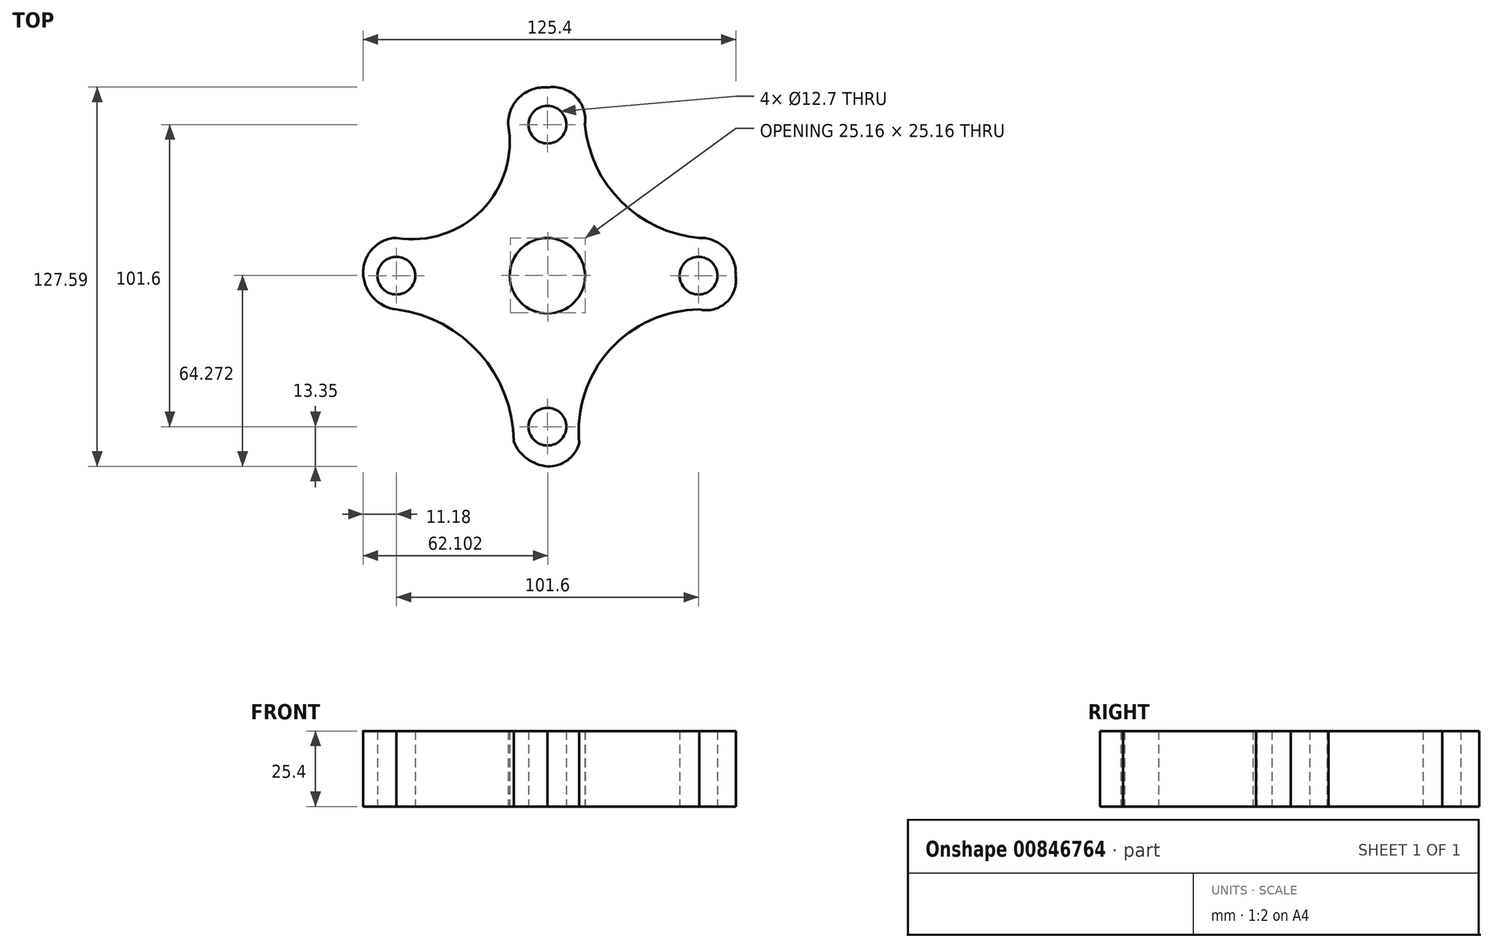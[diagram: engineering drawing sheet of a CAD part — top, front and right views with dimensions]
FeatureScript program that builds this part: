
annotation { "Feature Type Name" : "Feature", "Feature Type Description" : "" }
export const myFeature = defineFeature(function(context is Context, id is Id, definition is map)
    precondition{}
    {
        {
            var Q0;
            Q0=qCreatedBy(makeId("Top.planeOp"),FACE);
            var sketch = newSketch(context, id + "F0", { "sketchPlane" : qUnion([Q0])});
            skCircle(sketch, "E0", {"center": v(0, 0) * mm, "radius": 12.7 * mm});
            skLineSegment(sketch, "E1", {"start": v(0, 0) * mm, "end": v(50.8, 0) * mm});
            skLineSegment(sketch, "E2", {"start": v(0, 0) * mm, "end": v(-50.8, 0) * mm});
            skCircle(sketch, "E3", {"center": v(-50.8, 0) * mm, "radius": 6.35 * mm});
            skCircle(sketch, "E4", {"center": v(50.8, 0) * mm, "radius": 6.35 * mm});
            skLineSegment(sketch, "E5", {"start": v(0, 0) * mm, "end": v(0, 50.8) * mm});
            skLineSegment(sketch, "E6", {"start": v(0, 0) * mm, "end": v(0, -50.8) * mm});
            skCircle(sketch, "E7", {"center": v(0, 50.8) * mm, "radius": 6.35 * mm});
            skCircle(sketch, "E8", {"center": v(0, -50.8) * mm, "radius": 6.35 * mm});
            skArc(sketch, "E9", {"start": v(50.8, 0) * mm, "mid": v(47.62, -0.1) * mm, "end": v(44.46, -0.4) * mm});
            skArc(sketch, "E10.trimOffspring", {"start": v(0.4, -44.46) * mm, "mid": v(0.1, -47.62) * mm, "end": v(0, -50.8) * mm});
            skArc(sketch, "E11", {"start": v(-11.37, -55.83) * mm, "mid": v(-6.84, -61.57) * mm, "end": v(0, -64.15) * mm});
            skArc(sketch, "E12", {"start": v(0, -64.15) * mm, "mid": v(6.7, -62.1) * mm, "end": v(10.7, -56.34) * mm});
            skArc(sketch, "E13", {"start": v(51.08, -11.37) * mm, "mid": v(20.97, -24.95) * mm, "end": v(10.7, -56.34) * mm});
            skArc(sketch, "E14", {"start": v(51.08, -11.37) * mm, "mid": v(60.21, -8.94) * mm, "end": v(63.3, 0) * mm});
            skArc(sketch, "E15", {"start": v(63.3, 0) * mm, "mid": v(59.98, 9.05) * mm, "end": v(51.08, 12.73) * mm});
            skArc(sketch, "E16", {"start": v(12.56, 50.9) * mm, "mid": v(24.87, 24.81) * mm, "end": v(51.08, 12.73) * mm});
            skArc(sketch, "E17", {"start": v(12.56, 50.9) * mm, "mid": v(9.44, 60.3) * mm, "end": v(0, 63.3) * mm});
            skArc(sketch, "E18", {"start": v(0, 63.3) * mm, "mid": v(-9.38, 60.05) * mm, "end": v(-13.24, 50.9) * mm});
            skArc(sketch, "E19", {"start": v(-50.74, 12.73) * mm, "mid": v(-22.04, 22.04) * mm, "end": v(-13.24, 50.9) * mm});
            skArc(sketch, "E20", {"start": v(-50.74, 12.73) * mm, "mid": v(-59.07, 8.76) * mm, "end": v(-61.94, 0) * mm});
            skArc(sketch, "E21", {"start": v(-61.94, 0) * mm, "mid": v(-58.34, -7.66) * mm, "end": v(-50.74, -11.37) * mm});
            skArc(sketch, "E22", {"start": v(-11.37, -55.83) * mm, "mid": v(-22.71, -26.21) * mm, "end": v(-50.74, -11.37) * mm});
            skSolve(sketch);
        }
        {
            var Q0;
            Q0 = qSketchRegion(id + "F0", true);
            var Q1;
            {var subQ0=sQuery(id+"F0.wireOp",EDGE,"E5");var subQ1=sQuery(id+"F0.wireOp",EDGE,"E0");var subQ2=makeQuery(id+"F0.imprint","INTERSECT",VERTEX,{"derivedFrom":[subQ1,subQ0]});Q1=makeQuery(id+"F0.imprint","IMPRINT",FACE,{"disambiguationData":[TD([[makeQuery(id+"F0.imprint","IMPRINT",EDGE,{"disambiguationData":[TD([[subQ2,1.0]])],"derivedFrom":subQ1}),1.0]])]});}
            extrude(context, id + "F1", {"entities" : qUnion([Q0, Q1]), "depth" : 25.4 * mm, "offsetDistance" : 25.4 * mm});
        }
        {
            var Q0;
            Q0=makeQuery(id+"F1.opExtrude","CAP_FACE",FACE,{"disambiguationData":[OSD([sQuery(id+"F0.wireOp",EDGE,"E0"),sQuery(id+"F0.wireOp",EDGE,"E1"),sQuery(id+"F0.wireOp",EDGE,"E3"),sQuery(id+"F0.wireOp",EDGE,"E4"),sQuery(id+"F0.wireOp",EDGE,"E5"),sQuery(id+"F0.wireOp",EDGE,"E7"),sQuery(id+"F0.wireOp",EDGE,"E8"),sQuery(id+"F0.wireOp",EDGE,"E11"),sQuery(id+"F0.wireOp",EDGE,"E12"),sQuery(id+"F0.wireOp",EDGE,"E13"),sQuery(id+"F0.wireOp",EDGE,"E14"),sQuery(id+"F0.wireOp",EDGE,"E15"),sQuery(id+"F0.wireOp",EDGE,"E16"),sQuery(id+"F0.wireOp",EDGE,"E17"),sQuery(id+"F0.wireOp",EDGE,"E18"),sQuery(id+"F0.wireOp",EDGE,"E19"),sQuery(id+"F0.wireOp",EDGE,"E20"),sQuery(id+"F0.wireOp",EDGE,"E21"),sQuery(id+"F0.wireOp",EDGE,"E22")])],"isStart":false});
            var sketch = newSketch(context, id + "F2", { "sketchPlane" : qUnion([Q0])});
            skArc(sketch, "E23", {"start": v(12.7, 0) * mm, "mid": v(8.86, 8.86) * mm, "end": v(0, 12.7) * mm});
            skLineSegment(sketch, "E24", {"start": v(0, 0) * mm, "end": v(12.7, 0) * mm});
            skLineSegment(sketch, "E25", {"start": v(0, 0) * mm, "end": v(0, 12.7) * mm});
            skSolve(sketch);
        }
        {
            var Q0;
            Q0 = qSketchRegion(id + "F2", true);
            extrude(context, id + "F3", {"entities" : qUnion([Q0]), "operationType" : NewBodyOperationType.REMOVE, "oppositeDirection" : true, "depth" : 25.4 * mm, "offsetDistance" : 25.4 * mm});
        }
    });
